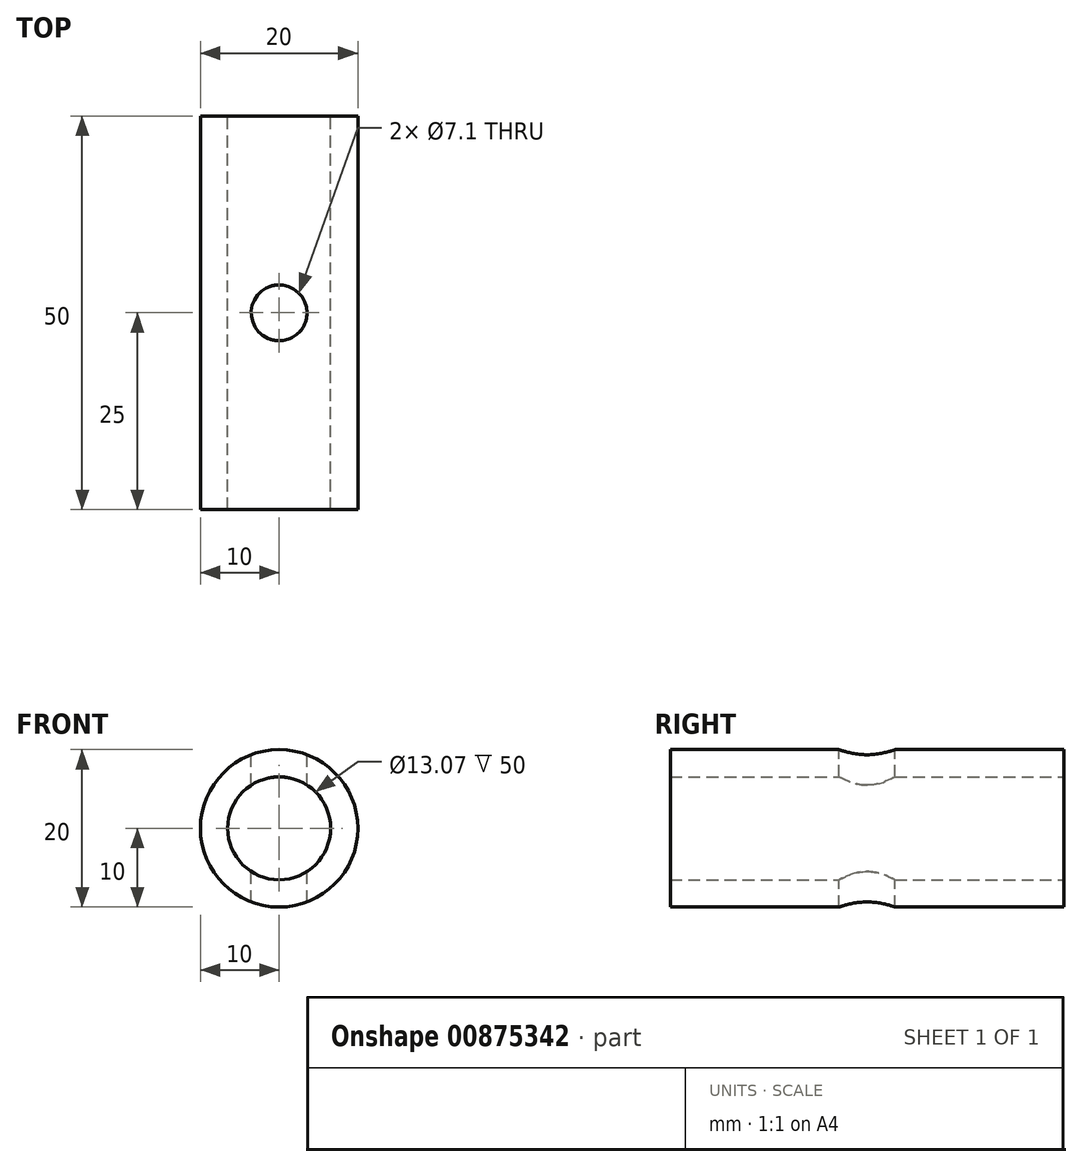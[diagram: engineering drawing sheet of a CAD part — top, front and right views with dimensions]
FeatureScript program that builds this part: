
annotation { "Feature Type Name" : "Feature", "Feature Type Description" : "" }
export const myFeature = defineFeature(function(context is Context, id is Id, definition is map)
    precondition{}
    {
        {
            var Q0;
            Q0=qCreatedBy(makeId("Front.planeOp"),FACE);
            var sketch = newSketch(context, id + "F0", { "sketchPlane" : qUnion([Q0])});
            skCircle(sketch, "E0", {"center": v(0, 0) * mm, "radius": 10 * mm});
            skSolve(sketch);
        }
        {
            var Q0;
            Q0=makeQuery(id+"F0.imprint","IMPRINT",FACE,{"disambiguationData":[TD([[makeQuery(id+"F0.imprint","IMPRINT",EDGE,{"derivedFrom":sQuery(id+"F0.wireOp",EDGE,"E0")}),1.0]])]});
            extrude(context, id + "F1", {"entities" : qUnion([Q0]), "depth" : 50 * mm, "offsetDistance" : 25 * mm});
        }
        {
            var Q0;
            Q0=qCreatedBy(makeId("Top.planeOp"),FACE);
            var sketch = newSketch(context, id + "F2", { "sketchPlane" : qUnion([Q0])});
            skCircle(sketch, "E1", {"center": v(0, -25) * mm, "radius": 3.55 * mm});
            skSolve(sketch);
        }
        {
            var Q0;
            Q0 = qSketchRegion(id + "F2", true);
            extrude(context, id + "F3", {"entities" : qUnion([Q0]), "operationType" : NewBodyOperationType.REMOVE, "oppositeDirection" : true, "depth" : 25 * mm, "offsetDistance" : 25 * mm, "hasSecondDirection" : true, "secondDirectionOppositeDirection" : false, "secondDirectionDepth" : 25 * mm});
        }
        {
            var Q0;
            Q0=makeQuery(id+"F1.opExtrude","CAP_FACE",FACE,{"disambiguationData":[OSD([sQuery(id+"F0.wireOp",EDGE,"E0")])],"isStart":true});
            var sketch = newSketch(context, id + "F4", { "sketchPlane" : qUnion([Q0])});
            skCircle(sketch, "E2", {"center": v(0, 0) * mm, "radius": 6.54 * mm});
            skSolve(sketch);
        }
        {
            var Q0;
            Q0=makeQuery(id+"F4.imprint","IMPRINT",FACE,{"disambiguationData":[TD([[makeQuery(id+"F4.imprint","IMPRINT",EDGE,{"derivedFrom":sQuery(id+"F4.wireOp",EDGE,"E2")}),1.0]])]});
            extrude(context, id + "F5", {"entities" : qUnion([Q0]), "operationType" : NewBodyOperationType.REMOVE, "oppositeDirection" : true, "depth" : 60 * mm, "offsetDistance" : 25 * mm});
        }
    });
